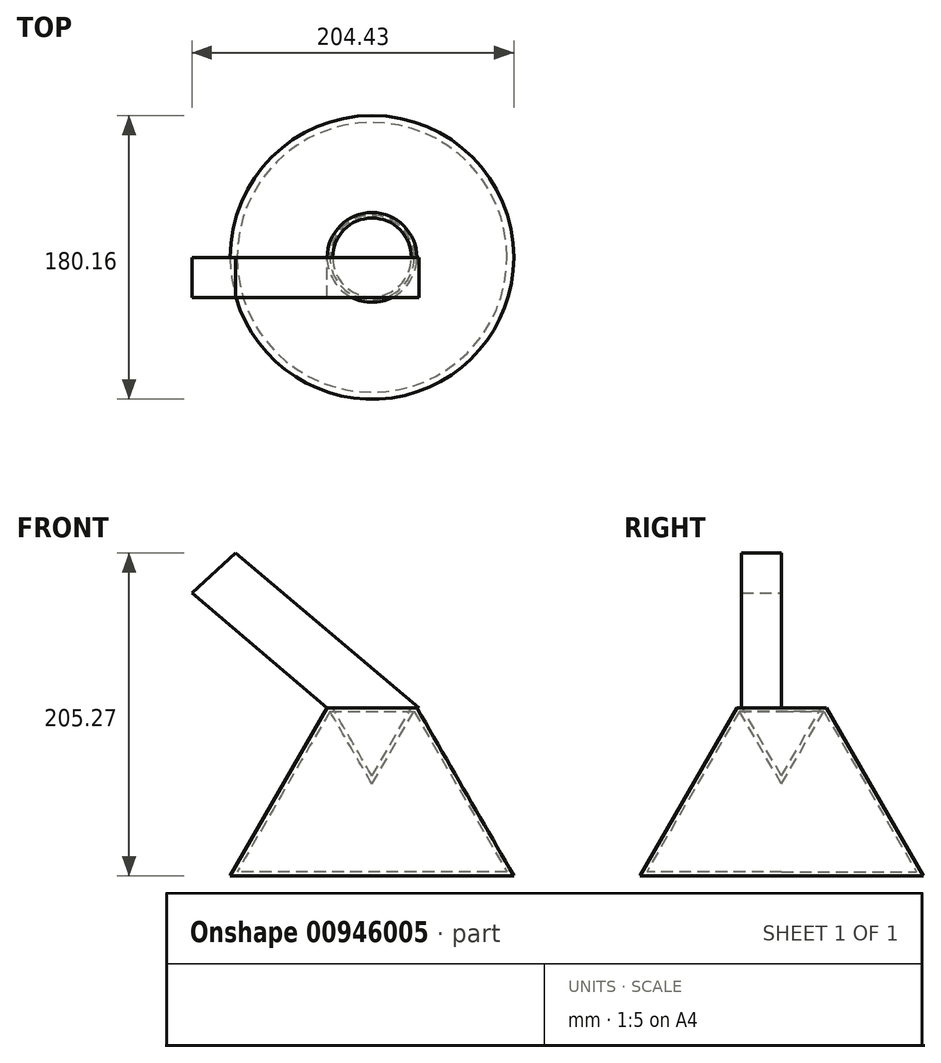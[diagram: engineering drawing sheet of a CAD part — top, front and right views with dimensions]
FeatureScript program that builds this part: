
annotation { "Feature Type Name" : "Feature", "Feature Type Description" : "" }
export const myFeature = defineFeature(function(context is Context, id is Id, definition is map)
    precondition{}
    {
        {
            var Q0;
            Q0=qCreatedBy(makeId("Top.planeOp"),FACE);
            var sketch = newSketch(context, id + "F0", { "sketchPlane" : qUnion([Q0])});
            skCircle(sketch, "E0", {"center": v(0, 0) * mm, "radius": 28.48 * mm});
            skCircle(sketch, "E1", {"center": v(0, 0) * mm, "radius": 25 * mm});
            skSolve(sketch);
        }
        {
            var Q0;
            Q0 = qSketchRegion(id + "F0", true);
            extrude(context, id + "F1", {"entities" : qUnion([Q0]), "oppositeDirection" : true, "depth" : 106.68 * mm, "offsetDistance" : 25.4 * mm, "hasDraft" : true, "draftAngle" : 30 * degree});
        }
        {
            var Q0;
            Q0=makeQuery(id+"F1.opExtrude","CAP_FACE",FACE,{"disambiguationData":[OSD([sQuery(id+"F0.wireOp",EDGE,"E0"),sQuery(id+"F0.wireOp",EDGE,"E1")])],"isStart":true});
            shell(context, id + "F2", {"entities" : qUnion([Q0]), "thickness" : 2.54 * mm});
        }
        {
            var Q0;
            Q0=qCreatedBy(makeId("Front.planeOp"),FACE);
            var sketch = newSketch(context, id + "F3", { "sketchPlane" : qUnion([Q0])});
            skLineSegment(sketch, "E2", {"start": v(29.85, 0) * mm, "end": v(-86.6, 98.59) * mm});
            skLineSegment(sketch, "E3", {"start": v(-28.59, 0) * mm, "end": v(-114.35, 72.94) * mm});
            skLineSegment(sketch, "E4", {"start": v(-114.35, 72.94) * mm, "end": v(-86.6, 98.59) * mm});
            skLineSegment(sketch, "E5", {"start": v(29.85, 0) * mm, "end": v(-28.59, 0) * mm});
            skSolve(sketch);
        }
        {
            var Q0;
            Q0 = qSketchRegion(id + "F3", true);
            extrude(context, id + "F4", {"entities" : qUnion([Q0]), "operationType" : NewBodyOperationType.ADD, "depth" : 25.4 * mm, "offsetDistance" : 25.4 * mm});
        }
    });
